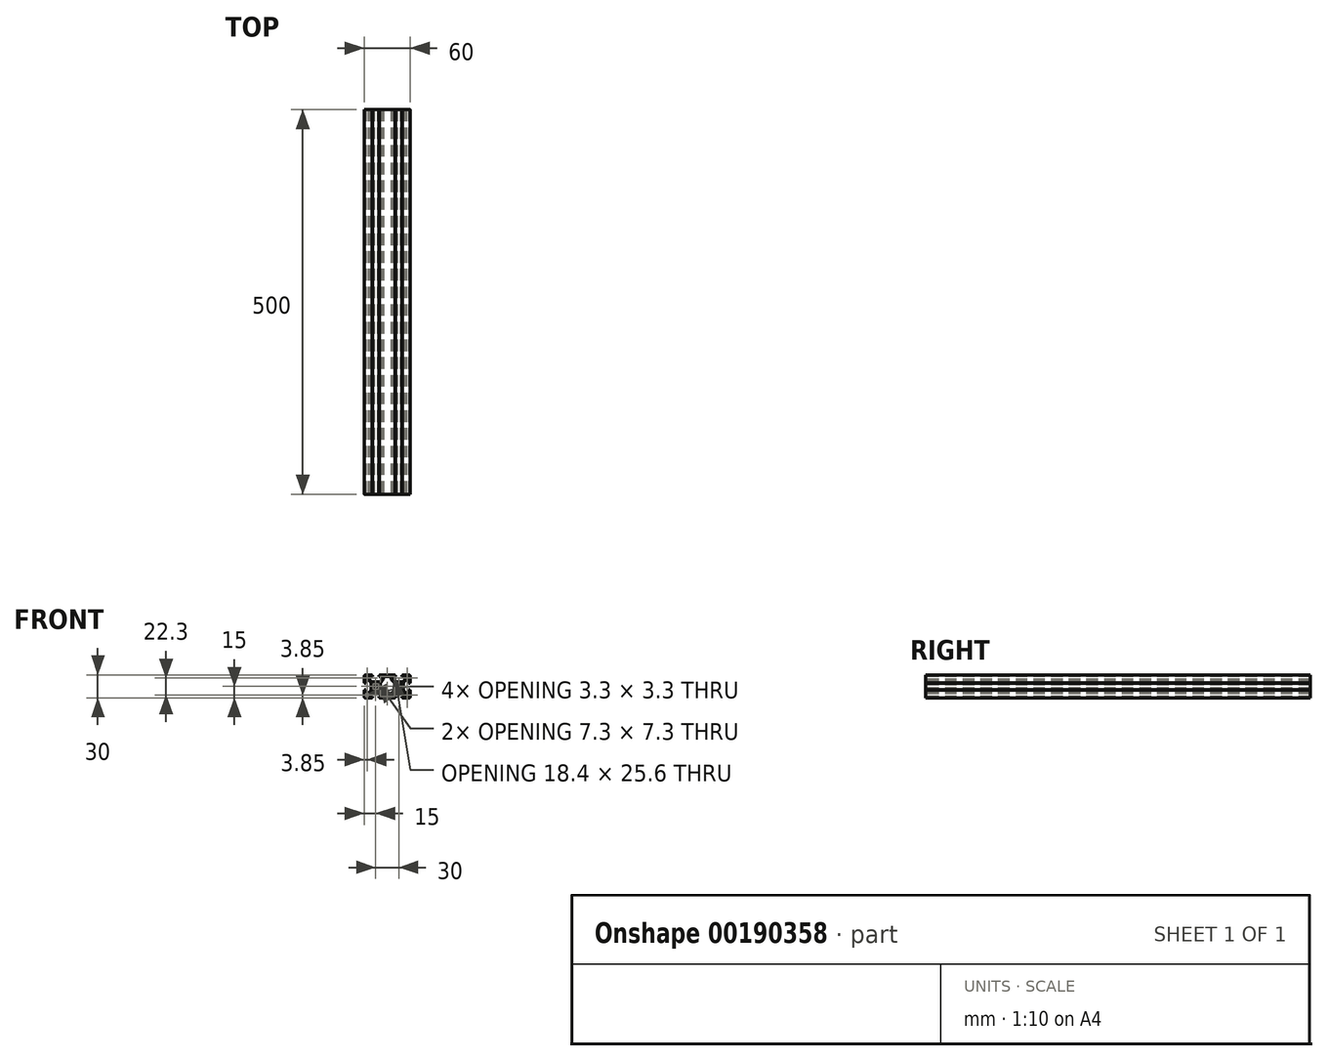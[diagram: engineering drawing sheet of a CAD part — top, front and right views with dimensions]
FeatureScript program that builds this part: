
annotation { "Feature Type Name" : "Feature", "Feature Type Description" : "" }
export const myFeature = defineFeature(function(context is Context, id is Id, definition is map)
    precondition{}
    {
        {
            var Q0;
            Q0=qCreatedBy(makeId("Front.planeOp"),FACE);
            var sketch = newSketch(context, id + "F0", { "sketchPlane" : qUnion([Q0])});
            skLineSegment(sketch, "E0.bottom", {"start": v(30, -15) * mm, "end": v(-30, -15) * mm});
            skLineSegment(sketch, "E0.top", {"start": v(30, 15) * mm, "end": v(-30, 15) * mm});
            skLineSegment(sketch, "E0.left", {"start": v(30, -15) * mm, "end": v(30, 15) * mm});
            skLineSegment(sketch, "E0.right", {"start": v(-30, -15) * mm, "end": v(-30, 15) * mm});
            skLineSegment(sketch, "E1", {"start": v(-30, -15) * mm, "end": v(30, 15) * mm, "construction": true});
            skSolve(sketch);
        }
        {
            var Q0;
            Q0 = qSketchRegion(id + "F0", true);
            extrude(context, id + "F1", {"entities" : qUnion([Q0]), "oppositeDirection" : true, "depth" : 500 * mm});
        }
        {
            var Q0;
            Q0=makeQuery(id+"F0.imprint","IMPRINT",FACE,{"disambiguationData":[TD([[makeQuery(id+"F0.imprint","IMPRINT",EDGE,{"derivedFrom":sQuery(id+"F0.wireOp",EDGE,"E0.bottom")}),-1.0]])]});
            var sketch = newSketch(context, id + "F2", { "sketchPlane" : qUnion([Q0])});
            skCircle(sketch, "E2", {"center": v(-15, 0) * mm, "radius": 3.65 * mm});
            skCircle(sketch, "E3.MirrorC", {"center": v(15, 0) * mm, "radius": 3.65 * mm});
            skSolve(sketch);
        }
        {
            var Q0;
            Q0 = qSketchRegion(id + "F2", true);
            extrude(context, id + "F3", {"entities" : qUnion([Q0]), "operationType" : NewBodyOperationType.REMOVE, "endBound" : BoundingType.THROUGH_ALL, "oppositeDirection" : true, "depth" : 25 * mm});
        }
        {
            var Q0;
            Q0=makeQuery(id+"F0.imprint","IMPRINT",FACE,{"disambiguationData":[TD([[makeQuery(id+"F0.imprint","IMPRINT",EDGE,{"derivedFrom":sQuery(id+"F0.wireOp",EDGE,"E0.bottom")}),-1.0]])]});
            var sketch = newSketch(context, id + "F4", { "sketchPlane" : qUnion([Q0])});
            skLineSegment(sketch, "E4", {"start": v(-15, 15) * mm, "end": v(-15, 0) * mm, "construction": true});
            skLineSegment(sketch, "E5", {"start": v(-15, 15) * mm, "end": v(-19, 15) * mm});
            skLineSegment(sketch, "E6", {"start": v(-19, 15) * mm, "end": v(-19, 12.8) * mm});
            skLineSegment(sketch, "E7", {"start": v(-19, 12.8) * mm, "end": v(-23, 12.8) * mm});
            skLineSegment(sketch, "E8", {"start": v(-23, 12.8) * mm, "end": v(-23, 8.8) * mm});
            skLineSegment(sketch, "E9", {"start": v(-20, 5.8) * mm, "end": v(-15, 5.8) * mm});
            skLineSegment(sketch, "E10.MirrorCS", {"start": v(-15, 15) * mm, "end": v(-11, 15) * mm});
            skLineSegment(sketch, "E11.MirrorCS", {"start": v(-11, 15) * mm, "end": v(-11, 12.8) * mm});
            skLineSegment(sketch, "E12.MirrorCS", {"start": v(-11, 12.8) * mm, "end": v(-7, 12.8) * mm});
            skLineSegment(sketch, "E13.MirrorCS", {"start": v(-10, 5.8) * mm, "end": v(-15, 5.8) * mm});
            skLineSegment(sketch, "E14.MirrorCS", {"start": v(-7, 12.8) * mm, "end": v(-7, 8.8) * mm});
            skLineSegment(sketch, "E15", {"start": v(0, 0) * mm, "end": v(0, 15) * mm, "construction": true});
            skLineSegment(sketch, "E16", {"start": v(0, 0) * mm, "end": v(-15, 0) * mm, "construction": true});
            skLineSegment(sketch, "E17", {"start": v(-20, 5.8) * mm, "end": v(-23, 8.8) * mm});
            skLineSegment(sketch, "E18.MirrorCS", {"start": v(-10, 5.8) * mm, "end": v(-7, 8.8) * mm});
            skLineSegment(sketch, "E19.MirrorCS", {"start": v(19, 15) * mm, "end": v(19, 12.8) * mm});
            skLineSegment(sketch, "E20.MirrorCS", {"start": v(11, 15) * mm, "end": v(11, 12.8) * mm});
            skLineSegment(sketch, "E21.MirrorCS", {"start": v(23, 12.8) * mm, "end": v(23, 8.8) * mm});
            skLineSegment(sketch, "E22.MirrorCS", {"start": v(20, 5.8) * mm, "end": v(15, 5.8) * mm});
            skLineSegment(sketch, "E23.MirrorCS", {"start": v(15, 15) * mm, "end": v(19, 15) * mm});
            skLineSegment(sketch, "E24.MirrorCS", {"start": v(7, 12.8) * mm, "end": v(7, 8.8) * mm});
            skLineSegment(sketch, "E25.MirrorCS", {"start": v(10, 5.8) * mm, "end": v(15, 5.8) * mm});
            skLineSegment(sketch, "E26.MirrorCS", {"start": v(19, 12.8) * mm, "end": v(23, 12.8) * mm});
            skLineSegment(sketch, "E27.MirrorCS", {"start": v(11, 12.8) * mm, "end": v(7, 12.8) * mm});
            skLineSegment(sketch, "E28.MirrorCS", {"start": v(15, 15) * mm, "end": v(11, 15) * mm});
            skLineSegment(sketch, "E29.MirrorCS", {"start": v(10, 5.8) * mm, "end": v(7, 8.8) * mm});
            skLineSegment(sketch, "E30.MirrorCS", {"start": v(20, 5.8) * mm, "end": v(23, 8.8) * mm});
            skLineSegment(sketch, "E31.1.0", {"start": v(20.8, 5) * mm, "end": v(23.8, 8) * mm});
            skLineSegment(sketch, "E31.1.1", {"start": v(30, 0) * mm, "end": v(30, -4) * mm});
            skLineSegment(sketch, "E31.1.2", {"start": v(27.8, -4) * mm, "end": v(27.8, -8) * mm});
            skLineSegment(sketch, "E31.1.3", {"start": v(27.8, -8) * mm, "end": v(23.8, -8) * mm});
            skLineSegment(sketch, "E31.1.4", {"start": v(30, 0) * mm, "end": v(30, 4) * mm});
            skLineSegment(sketch, "E31.1.5", {"start": v(27.8, 4) * mm, "end": v(27.8, 8) * mm});
            skLineSegment(sketch, "E31.1.6", {"start": v(20.8, 5) * mm, "end": v(20.8, 0) * mm});
            skLineSegment(sketch, "E31.1.7", {"start": v(27.8, 8) * mm, "end": v(23.8, 8) * mm});
            skLineSegment(sketch, "E31.1.8", {"start": v(20.8, -5) * mm, "end": v(20.8, 0) * mm});
            skLineSegment(sketch, "E31.1.9", {"start": v(20.8, -5) * mm, "end": v(23.8, -8) * mm});
            skLineSegment(sketch, "E31.1.10", {"start": v(27.8, 8) * mm, "end": v(23.8, 8) * mm});
            skLineSegment(sketch, "E31.1.11", {"start": v(20.8, -5) * mm, "end": v(20.8, 0) * mm});
            skLineSegment(sketch, "E31.1.12", {"start": v(20.8, 5) * mm, "end": v(20.8, 0) * mm});
            skLineSegment(sketch, "E31.1.13", {"start": v(30, 0) * mm, "end": v(30, -4) * mm});
            skLineSegment(sketch, "E31.1.14", {"start": v(27.8, 4) * mm, "end": v(27.8, 8) * mm});
            skLineSegment(sketch, "E31.1.15", {"start": v(27.8, -4) * mm, "end": v(27.8, -8) * mm});
            skLineSegment(sketch, "E31.1.16", {"start": v(27.8, -8) * mm, "end": v(23.8, -8) * mm});
            skLineSegment(sketch, "E31.1.17", {"start": v(30, 0) * mm, "end": v(30, 4) * mm});
            skLineSegment(sketch, "E31.1.18", {"start": v(30, 4) * mm, "end": v(27.8, 4) * mm});
            skLineSegment(sketch, "E31.1.19", {"start": v(30, -4) * mm, "end": v(27.8, -4) * mm});
            skLineSegment(sketch, "E31.1.20", {"start": v(30, 4) * mm, "end": v(27.8, 4) * mm});
            skLineSegment(sketch, "E31.1.21", {"start": v(30, -4) * mm, "end": v(27.8, -4) * mm});
            skLineSegment(sketch, "E31.2.0", {"start": v(20, -5.8) * mm, "end": v(23, -8.8) * mm});
            skLineSegment(sketch, "E31.2.1", {"start": v(15, -15) * mm, "end": v(11, -15) * mm});
            skLineSegment(sketch, "E31.2.2", {"start": v(11, -12.8) * mm, "end": v(7, -12.8) * mm});
            skLineSegment(sketch, "E31.2.3", {"start": v(7, -12.8) * mm, "end": v(7, -8.8) * mm});
            skLineSegment(sketch, "E31.2.4", {"start": v(15, -15) * mm, "end": v(19, -15) * mm});
            skLineSegment(sketch, "E31.2.5", {"start": v(19, -12.8) * mm, "end": v(23, -12.8) * mm});
            skLineSegment(sketch, "E31.2.6", {"start": v(20, -5.8) * mm, "end": v(15, -5.8) * mm});
            skLineSegment(sketch, "E31.2.7", {"start": v(23, -12.8) * mm, "end": v(23, -8.8) * mm});
            skLineSegment(sketch, "E31.2.8", {"start": v(10, -5.8) * mm, "end": v(15, -5.8) * mm});
            skLineSegment(sketch, "E31.2.9", {"start": v(10, -5.8) * mm, "end": v(7, -8.8) * mm});
            skLineSegment(sketch, "E31.2.10", {"start": v(23, -12.8) * mm, "end": v(23, -8.8) * mm});
            skLineSegment(sketch, "E31.2.11", {"start": v(10, -5.8) * mm, "end": v(15, -5.8) * mm});
            skLineSegment(sketch, "E31.2.12", {"start": v(20, -5.8) * mm, "end": v(15, -5.8) * mm});
            skLineSegment(sketch, "E31.2.13", {"start": v(15, -15) * mm, "end": v(11, -15) * mm});
            skLineSegment(sketch, "E31.2.14", {"start": v(19, -12.8) * mm, "end": v(23, -12.8) * mm});
            skLineSegment(sketch, "E31.2.15", {"start": v(11, -12.8) * mm, "end": v(7, -12.8) * mm});
            skLineSegment(sketch, "E31.2.16", {"start": v(7, -12.8) * mm, "end": v(7, -8.8) * mm});
            skLineSegment(sketch, "E31.2.17", {"start": v(15, -15) * mm, "end": v(19, -15) * mm});
            skLineSegment(sketch, "E31.2.18", {"start": v(19, -15) * mm, "end": v(19, -12.8) * mm});
            skLineSegment(sketch, "E31.2.19", {"start": v(11, -15) * mm, "end": v(11, -12.8) * mm});
            skLineSegment(sketch, "E31.2.20", {"start": v(19, -15) * mm, "end": v(19, -12.8) * mm});
            skLineSegment(sketch, "E31.2.21", {"start": v(11, -15) * mm, "end": v(11, -12.8) * mm});
            skPoint(sketch, "E31.center", {"position": v(15, 0) * mm});
            skLineSegment(sketch, "E31.anchor1", {"start": v(15, 0) * mm, "end": v(7, 8.8) * mm, "construction": true});
            skLineSegment(sketch, "E31.anchor2", {"start": v(15, 0) * mm, "end": v(23, -8.8) * mm, "construction": true});
            skLineSegment(sketch, "E32.MirrorCS", {"start": v(-20.8, 5) * mm, "end": v(-20.8, 0) * mm});
            skLineSegment(sketch, "E33.MirrorCS", {"start": v(-20.8, 5) * mm, "end": v(-23.8, 8) * mm});
            skLineSegment(sketch, "E34.MirrorCS", {"start": v(-27.8, 8) * mm, "end": v(-23.8, 8) * mm});
            skLineSegment(sketch, "E35.MirrorCS", {"start": v(-27.8, 4) * mm, "end": v(-27.8, 8) * mm});
            skLineSegment(sketch, "E36.MirrorCS", {"start": v(-30, 4) * mm, "end": v(-27.8, 4) * mm});
            skLineSegment(sketch, "E37.MirrorCS", {"start": v(-30, 0) * mm, "end": v(-30, 4) * mm});
            skLineSegment(sketch, "E38.MirrorCS", {"start": v(-30, 0) * mm, "end": v(-30, -4) * mm});
            skLineSegment(sketch, "E39.MirrorCS", {"start": v(-30, -4) * mm, "end": v(-27.8, -4) * mm});
            skLineSegment(sketch, "E40.MirrorCS", {"start": v(-27.8, -4) * mm, "end": v(-27.8, -8) * mm});
            skLineSegment(sketch, "E41.MirrorCS", {"start": v(-27.8, -8) * mm, "end": v(-23.8, -8) * mm});
            skLineSegment(sketch, "E42.MirrorCS", {"start": v(-20.8, -5) * mm, "end": v(-23.8, -8) * mm});
            skLineSegment(sketch, "E43.MirrorCS", {"start": v(-20.8, -5) * mm, "end": v(-20.8, 0) * mm});
            skLineSegment(sketch, "E44.MirrorCS", {"start": v(-19, -12.8) * mm, "end": v(-23, -12.8) * mm});
            skLineSegment(sketch, "E45.MirrorCS", {"start": v(-23, -12.8) * mm, "end": v(-23, -8.8) * mm});
            skLineSegment(sketch, "E46.MirrorCS", {"start": v(-11, -12.8) * mm, "end": v(-7, -12.8) * mm});
            skLineSegment(sketch, "E47.MirrorCS", {"start": v(-10, -5.8) * mm, "end": v(-15, -5.8) * mm});
            skLineSegment(sketch, "E48.MirrorCS", {"start": v(-20, -5.8) * mm, "end": v(-15, -5.8) * mm});
            skLineSegment(sketch, "E49.MirrorCS", {"start": v(-15, -15) * mm, "end": v(-19, -15) * mm});
            skLineSegment(sketch, "E50.MirrorCS", {"start": v(-19, -15) * mm, "end": v(-19, -12.8) * mm});
            skLineSegment(sketch, "E51.MirrorCS", {"start": v(-15, -15) * mm, "end": v(-11, -15) * mm});
            skLineSegment(sketch, "E52.MirrorCS", {"start": v(-11, -15) * mm, "end": v(-11, -12.8) * mm});
            skLineSegment(sketch, "E53.MirrorCS", {"start": v(-7, -12.8) * mm, "end": v(-7, -8.8) * mm});
            skLineSegment(sketch, "E54.MirrorCS", {"start": v(-20, -5.8) * mm, "end": v(-23, -8.8) * mm});
            skLineSegment(sketch, "E55.MirrorCS", {"start": v(-10, -5.8) * mm, "end": v(-7, -8.8) * mm});
            skLineSegment(sketch, "E56.MirrorCS", {"start": v(-9.2, 5) * mm, "end": v(-9.2, 0) * mm});
            skLineSegment(sketch, "E57.MirrorCS", {"start": v(-9.2, -5) * mm, "end": v(-9.2, 0) * mm});
            skLineSegment(sketch, "E58", {"start": v(-9.2, 5) * mm, "end": v(-5.3, 8.9) * mm});
            skLineSegment(sketch, "E59", {"start": v(-5.3, 8.9) * mm, "end": v(-5.3, 12.8) * mm});
            skLineSegment(sketch, "E60", {"start": v(-5.3, 12.8) * mm, "end": v(0, 12.8) * mm});
            skLineSegment(sketch, "E61.MirrorCS", {"start": v(-5.3, -12.8) * mm, "end": v(0, -12.8) * mm});
            skLineSegment(sketch, "E62.MirrorCS", {"start": v(-5.3, -8.9) * mm, "end": v(-5.3, -12.8) * mm});
            skLineSegment(sketch, "E63.MirrorCS", {"start": v(-9.2, -5) * mm, "end": v(-5.3, -8.9) * mm});
            skLineSegment(sketch, "E64.MirrorCS", {"start": v(5.3, 12.8) * mm, "end": v(0, 12.8) * mm});
            skLineSegment(sketch, "E65.MirrorCS", {"start": v(5.3, 8.9) * mm, "end": v(5.3, 12.8) * mm});
            skLineSegment(sketch, "E66.MirrorCS", {"start": v(9.2, 5) * mm, "end": v(5.3, 8.9) * mm});
            skLineSegment(sketch, "E67.MirrorCS", {"start": v(9.2, 5) * mm, "end": v(9.2, 0) * mm});
            skLineSegment(sketch, "E68.MirrorCS", {"start": v(9.2, -5) * mm, "end": v(9.2, 0) * mm});
            skLineSegment(sketch, "E69.MirrorCS", {"start": v(9.2, -5) * mm, "end": v(5.3, -8.9) * mm});
            skLineSegment(sketch, "E70.MirrorCS", {"start": v(5.3, -12.8) * mm, "end": v(0, -12.8) * mm});
            skLineSegment(sketch, "E71.MirrorCS", {"start": v(5.3, -8.9) * mm, "end": v(5.3, -12.8) * mm});
            skSolve(sketch);
        }
        {
            var Q0;
            Q0 = qSketchRegion(id + "F4", true);
            extrude(context, id + "F5", {"entities" : qUnion([Q0]), "operationType" : NewBodyOperationType.REMOVE, "endBound" : BoundingType.THROUGH_ALL, "oppositeDirection" : true, "depth" : 25 * mm});
        }
        {
            var Q0;
            Q0=makeQuery(id+"F1.opExtrude","SWEPT_EDGE",EDGE,{"disambiguationData":[OSD([sQuery(id+"F0.wireOp",EDGE,"E0.top"),sQuery(id+"F0.wireOp",EDGE,"E0.right")])]});
            var Q1;
            Q1=makeQuery(id+"F1.opExtrude","SWEPT_EDGE",EDGE,{"disambiguationData":[OSD([sQuery(id+"F0.wireOp",EDGE,"E0.top"),sQuery(id+"F0.wireOp",EDGE,"E0.left")])]});
            var Q2;
            Q2=makeQuery(id+"F1.opExtrude","SWEPT_EDGE",EDGE,{"disambiguationData":[OSD([sQuery(id+"F0.wireOp",EDGE,"E0.bottom"),sQuery(id+"F0.wireOp",EDGE,"E0.left")])]});
            var Q3;
            Q3=makeQuery(id+"F1.opExtrude","SWEPT_EDGE",EDGE,{"disambiguationData":[OSD([sQuery(id+"F0.wireOp",EDGE,"E0.bottom"),sQuery(id+"F0.wireOp",EDGE,"E0.right")])]});
            fillet(context, id + "F6", {"entities" : qUnion([Q0, Q1, Q2, Q3]), "radius" : 2 * mm, "tangentPropagation" : true, "allowEdgeOverflow" : false});
        }
        {
            var Q0;
            Q0=makeQuery(id+"F1.opExtrude","CAP_FACE",FACE,{"disambiguationData":[OSD([sQuery(id+"F0.wireOp",EDGE,"E0.bottom"),sQuery(id+"F0.wireOp",EDGE,"E0.top"),sQuery(id+"F0.wireOp",EDGE,"E0.left"),sQuery(id+"F0.wireOp",EDGE,"E0.right")])],"isStart":true});
            var sketch = newSketch(context, id + "F7", { "sketchPlane" : qUnion([Q0])});
            skLineSegment(sketch, "E72", {"start": v(-24.5, 9.5) * mm, "end": v(-27.8, 9.5) * mm});
            skLineSegment(sketch, "E73", {"start": v(-27.8, 9.5) * mm, "end": v(-27.8, 11.8) * mm});
            skLineSegment(sketch, "E74", {"start": v(-26.8, 12.8) * mm, "end": v(-24.5, 12.8) * mm});
            skLineSegment(sketch, "E75", {"start": v(-24.5, 12.8) * mm, "end": v(-24.5, 9.5) * mm});
            skPoint(sketch, "E76.visualSharp", {"position": v(-27.8, 12.8) * mm});
            skArc(sketch, "E76.filletArc", {"start": v(-26.8, 12.8) * mm, "mid": v(-27.5, 12.5) * mm, "end": v(-27.8, 11.8) * mm});
            skLineSegment(sketch, "E77", {"start": v(0, 0) * mm, "end": v(0, 17.26) * mm, "construction": true});
            skPoint(sketch, "E77.endSnap0", {"position": v(0, 15) * mm});
            skLineSegment(sketch, "E78", {"start": v(0, 0) * mm, "end": v(-33.03, 0) * mm, "construction": true});
            skLineSegment(sketch, "E79.MirrorCS", {"start": v(24.5, 12.8) * mm, "end": v(24.5, 9.5) * mm});
            skArc(sketch, "E80.MirrorCS", {"start": v(26.8, 12.8) * mm, "mid": v(27.5, 12.5) * mm, "end": v(27.8, 11.8) * mm});
            skPoint(sketch, "E81.MirrorP", {"position": v(27.8, 12.8) * mm});
            skLineSegment(sketch, "E82.MirrorCS", {"start": v(24.5, 9.5) * mm, "end": v(27.8, 9.5) * mm});
            skLineSegment(sketch, "E83.MirrorCS", {"start": v(27.8, 9.5) * mm, "end": v(27.8, 11.8) * mm});
            skLineSegment(sketch, "E84.MirrorCS", {"start": v(26.8, 12.8) * mm, "end": v(24.5, 12.8) * mm});
            skArc(sketch, "E85.MirrorCS", {"start": v(26.8, -12.8) * mm, "mid": v(27.5, -12.5) * mm, "end": v(27.8, -11.8) * mm});
            skLineSegment(sketch, "E86.MirrorCS", {"start": v(-27.8, -9.5) * mm, "end": v(-27.8, -11.8) * mm});
            skArc(sketch, "E87.MirrorCS", {"start": v(-26.8, -12.8) * mm, "mid": v(-27.5, -12.5) * mm, "end": v(-27.8, -11.8) * mm});
            skLineSegment(sketch, "E88.MirrorCS", {"start": v(-24.5, -12.8) * mm, "end": v(-24.5, -9.5) * mm});
            skPoint(sketch, "E89.MirrorP", {"position": v(27.8, -12.8) * mm});
            skPoint(sketch, "E90.MirrorP", {"position": v(-27.8, -12.8) * mm});
            skPoint(sketch, "E91.MirrorP", {"position": v(0, -15) * mm});
            skLineSegment(sketch, "E92.MirrorCS", {"start": v(26.8, -12.8) * mm, "end": v(24.5, -12.8) * mm});
            skLineSegment(sketch, "E93.MirrorCS", {"start": v(-24.5, -9.5) * mm, "end": v(-27.8, -9.5) * mm});
            skLineSegment(sketch, "E94.MirrorCS", {"start": v(27.8, -9.5) * mm, "end": v(27.8, -11.8) * mm});
            skLineSegment(sketch, "E95.MirrorCS", {"start": v(24.5, -9.5) * mm, "end": v(27.8, -9.5) * mm});
            skLineSegment(sketch, "E96.MirrorCS", {"start": v(24.5, -12.8) * mm, "end": v(24.5, -9.5) * mm});
            skLineSegment(sketch, "E97.MirrorCS", {"start": v(-26.8, -12.8) * mm, "end": v(-24.5, -12.8) * mm});
            skSolve(sketch);
        }
        {
            var Q0;
            Q0 = qSketchRegion(id + "F7", true);
            extrude(context, id + "F8", {"entities" : qUnion([Q0]), "operationType" : NewBodyOperationType.REMOVE, "endBound" : BoundingType.THROUGH_ALL, "oppositeDirection" : true, "depth" : 25 * mm});
        }
        {
            var Q0;
            Q0=makeQuery(id+"F1.opExtrude","CAP_FACE",FACE,{"disambiguationData":[OSD([sQuery(id+"F0.wireOp",EDGE,"E0.bottom"),sQuery(id+"F0.wireOp",EDGE,"E0.top"),sQuery(id+"F0.wireOp",EDGE,"E0.left"),sQuery(id+"F0.wireOp",EDGE,"E0.right")])],"isStart":true});
            var sketch = newSketch(context, id + "F9", { "sketchPlane" : qUnion([Q0])});
            skLineSegment(sketch, "E98", {"start": v(-15, 0) * mm, "end": v(-15, 5.8) * mm, "construction": true});
            skLineSegment(sketch, "E99", {"start": v(-15, 0) * mm, "end": v(-20.8, 5.8) * mm, "construction": true});
            skLineSegment(sketch, "E100", {"start": v(-17.95, 2.15) * mm, "end": v(-18.64, 2.84) * mm});
            skLineSegment(sketch, "E101", {"start": v(-17.22, 2.9) * mm, "end": v(-17.9, 3.58) * mm});
            skPoint(sketch, "E101.startSnap0", {"position": v(-17.9, 2.9) * mm});
            skPoint(sketch, "E101.endSnap0", {"position": v(-17.9, 2.9) * mm});
            skLineSegment(sketch, "E102", {"start": v(-17.9, 3.58) * mm, "end": v(-18.64, 2.84) * mm});
            skLineSegment(sketch, "E103", {"start": v(-17.95, 2.15) * mm, "end": v(-17.22, 2.9) * mm});
            skLineSegment(sketch, "E104.1.0", {"start": v(-17.15, -2.95) * mm, "end": v(-17.84, -3.64) * mm});
            skLineSegment(sketch, "E104.1.1", {"start": v(-18.58, -2.9) * mm, "end": v(-17.84, -3.64) * mm});
            skLineSegment(sketch, "E104.1.2", {"start": v(-17.9, -2.22) * mm, "end": v(-18.58, -2.9) * mm});
            skLineSegment(sketch, "E104.1.3", {"start": v(-17.15, -2.95) * mm, "end": v(-17.9, -2.22) * mm});
            skLineSegment(sketch, "E104.2.0", {"start": v(-12.05, -2.15) * mm, "end": v(-11.36, -2.84) * mm});
            skLineSegment(sketch, "E104.2.1", {"start": v(-12.1, -3.58) * mm, "end": v(-11.36, -2.84) * mm});
            skLineSegment(sketch, "E104.2.2", {"start": v(-12.78, -2.9) * mm, "end": v(-12.1, -3.58) * mm});
            skLineSegment(sketch, "E104.2.3", {"start": v(-12.05, -2.15) * mm, "end": v(-12.78, -2.9) * mm});
            skLineSegment(sketch, "E104.3.0", {"start": v(-12.85, 2.95) * mm, "end": v(-12.16, 3.64) * mm});
            skLineSegment(sketch, "E104.3.1", {"start": v(-11.42, 2.9) * mm, "end": v(-12.16, 3.64) * mm});
            skLineSegment(sketch, "E104.3.2", {"start": v(-12.1, 2.22) * mm, "end": v(-11.42, 2.9) * mm});
            skLineSegment(sketch, "E104.3.3", {"start": v(-12.85, 2.95) * mm, "end": v(-12.1, 2.22) * mm});
            skPoint(sketch, "E104.center", {"position": v(-15, 0) * mm});
            skLineSegment(sketch, "E105", {"start": v(0, 0) * mm, "end": v(0, 16.82) * mm, "construction": true});
            skPoint(sketch, "E105.endSnap0", {"position": v(0, 15) * mm});
            skLineSegment(sketch, "E106.MirrorCS", {"start": v(12.1, 2.22) * mm, "end": v(11.42, 2.9) * mm});
            skLineSegment(sketch, "E107.MirrorCS", {"start": v(11.42, 2.9) * mm, "end": v(12.16, 3.64) * mm});
            skLineSegment(sketch, "E108.MirrorCS", {"start": v(12.85, 2.95) * mm, "end": v(12.16, 3.64) * mm});
            skLineSegment(sketch, "E109.MirrorCS", {"start": v(12.85, 2.95) * mm, "end": v(12.1, 2.22) * mm});
            skLineSegment(sketch, "E110.MirrorCS", {"start": v(17.95, 2.15) * mm, "end": v(17.22, 2.9) * mm});
            skLineSegment(sketch, "E111.MirrorCS", {"start": v(17.22, 2.9) * mm, "end": v(17.9, 3.58) * mm});
            skLineSegment(sketch, "E112.MirrorCS", {"start": v(17.9, 3.58) * mm, "end": v(18.64, 2.84) * mm});
            skLineSegment(sketch, "E113.MirrorCS", {"start": v(17.95, 2.15) * mm, "end": v(18.64, 2.84) * mm});
            skLineSegment(sketch, "E114.MirrorCS", {"start": v(18.58, -2.9) * mm, "end": v(17.84, -3.64) * mm});
            skLineSegment(sketch, "E115.MirrorCS", {"start": v(17.9, -2.22) * mm, "end": v(18.58, -2.9) * mm});
            skLineSegment(sketch, "E116.MirrorCS", {"start": v(17.15, -2.95) * mm, "end": v(17.9, -2.22) * mm});
            skLineSegment(sketch, "E117.MirrorCS", {"start": v(17.15, -2.95) * mm, "end": v(17.84, -3.64) * mm});
            skLineSegment(sketch, "E118.MirrorCS", {"start": v(12.05, -2.15) * mm, "end": v(11.36, -2.84) * mm});
            skLineSegment(sketch, "E119.MirrorCS", {"start": v(12.05, -2.15) * mm, "end": v(12.78, -2.9) * mm});
            skLineSegment(sketch, "E120.MirrorCS", {"start": v(12.78, -2.9) * mm, "end": v(12.1, -3.58) * mm});
            skLineSegment(sketch, "E121.MirrorCS", {"start": v(12.1, -3.58) * mm, "end": v(11.36, -2.84) * mm});
            skSolve(sketch);
        }
        {
            var Q0;
            Q0 = qSketchRegion(id + "F9", true);
            extrude(context, id + "F10", {"entities" : qUnion([Q0]), "operationType" : NewBodyOperationType.REMOVE, "endBound" : BoundingType.THROUGH_ALL, "oppositeDirection" : true, "depth" : 25 * mm});
        }
        {
            var Q0;
            Q0=makeQuery(id+"F1.opExtrude","CAP_FACE",FACE,{"disambiguationData":[OSD([sQuery(id+"F0.wireOp",EDGE,"E0.bottom"),sQuery(id+"F0.wireOp",EDGE,"E0.top"),sQuery(id+"F0.wireOp",EDGE,"E0.left"),sQuery(id+"F0.wireOp",EDGE,"E0.right")])],"isStart":true});
            var sketch = newSketch(context, id + "F11", { "sketchPlane" : qUnion([Q0])});
            skLineSegment(sketch, "E122.bottom", {"start": v(11, 15) * mm, "end": v(10.2, 15) * mm});
            skLineSegment(sketch, "E122.top", {"start": v(11, 14.2) * mm, "end": v(10.2, 14.2) * mm});
            skLineSegment(sketch, "E122.left", {"start": v(11, 15) * mm, "end": v(11, 14.2) * mm});
            skLineSegment(sketch, "E122.right", {"start": v(10.2, 15) * mm, "end": v(10.2, 14.2) * mm});
            skLineSegment(sketch, "E123.bottom", {"start": v(19, 15) * mm, "end": v(19.8, 15) * mm});
            skLineSegment(sketch, "E123.top", {"start": v(19, 14.2) * mm, "end": v(19.8, 14.2) * mm});
            skLineSegment(sketch, "E123.left", {"start": v(19, 15) * mm, "end": v(19, 14.2) * mm});
            skLineSegment(sketch, "E123.right", {"start": v(19.8, 15) * mm, "end": v(19.8, 14.2) * mm});
            skLineSegment(sketch, "E124.1.0", {"start": v(30, -4) * mm, "end": v(30, -4.8) * mm});
            skLineSegment(sketch, "E124.1.1", {"start": v(29.2, -4) * mm, "end": v(29.2, -4.8) * mm});
            skLineSegment(sketch, "E124.1.2", {"start": v(30, 4) * mm, "end": v(30, 4.8) * mm});
            skLineSegment(sketch, "E124.1.3", {"start": v(29.2, 4) * mm, "end": v(29.2, 4.8) * mm});
            skLineSegment(sketch, "E124.1.4", {"start": v(30, 4) * mm, "end": v(29.2, 4) * mm});
            skLineSegment(sketch, "E124.1.5", {"start": v(30, 4.8) * mm, "end": v(29.2, 4.8) * mm});
            skLineSegment(sketch, "E124.1.6", {"start": v(30, -4.8) * mm, "end": v(29.2, -4.8) * mm});
            skLineSegment(sketch, "E124.1.7", {"start": v(30, -4) * mm, "end": v(29.2, -4) * mm});
            skLineSegment(sketch, "E124.2.0", {"start": v(11, -15) * mm, "end": v(10.2, -15) * mm});
            skLineSegment(sketch, "E124.2.1", {"start": v(11, -14.2) * mm, "end": v(10.2, -14.2) * mm});
            skLineSegment(sketch, "E124.2.2", {"start": v(19, -15) * mm, "end": v(19.8, -15) * mm});
            skLineSegment(sketch, "E124.2.3", {"start": v(19, -14.2) * mm, "end": v(19.8, -14.2) * mm});
            skLineSegment(sketch, "E124.2.4", {"start": v(19, -15) * mm, "end": v(19, -14.2) * mm});
            skLineSegment(sketch, "E124.2.5", {"start": v(19.8, -15) * mm, "end": v(19.8, -14.2) * mm});
            skLineSegment(sketch, "E124.2.6", {"start": v(10.2, -15) * mm, "end": v(10.2, -14.2) * mm});
            skLineSegment(sketch, "E124.2.7", {"start": v(11, -15) * mm, "end": v(11, -14.2) * mm});
            skPoint(sketch, "E124.center", {"position": v(15, 0) * mm});
            skLineSegment(sketch, "E124.anchor1", {"start": v(15, 0) * mm, "end": v(10.2, 14.2) * mm, "construction": true});
            skLineSegment(sketch, "E124.anchor2", {"start": v(15, 0) * mm, "end": v(19.8, -14.2) * mm, "construction": true});
            skLineSegment(sketch, "E125", {"start": v(0, 0) * mm, "end": v(0, 17.97) * mm, "construction": true});
            skPoint(sketch, "E125.endSnap0", {"position": v(0, 15) * mm});
            skLineSegment(sketch, "E126.MirrorCS", {"start": v(-11, 14.2) * mm, "end": v(-10.2, 14.2) * mm});
            skLineSegment(sketch, "E127.MirrorCS", {"start": v(-19.8, 15) * mm, "end": v(-19.8, 14.2) * mm});
            skLineSegment(sketch, "E128.MirrorCS", {"start": v(-19, 15) * mm, "end": v(-19, 14.2) * mm});
            skLineSegment(sketch, "E129.MirrorCS", {"start": v(-19, 14.2) * mm, "end": v(-19.8, 14.2) * mm});
            skLineSegment(sketch, "E130.MirrorCS", {"start": v(-19, 15) * mm, "end": v(-19.8, 15) * mm});
            skLineSegment(sketch, "E131.MirrorCS", {"start": v(-10.2, 15) * mm, "end": v(-10.2, 14.2) * mm});
            skLineSegment(sketch, "E132.MirrorCS", {"start": v(-11, 15) * mm, "end": v(-11, 14.2) * mm});
            skLineSegment(sketch, "E133.MirrorCS", {"start": v(-11, 15) * mm, "end": v(-10.2, 15) * mm});
            skLineSegment(sketch, "E134.MirrorCS", {"start": v(-30, 4) * mm, "end": v(-29.2, 4) * mm});
            skLineSegment(sketch, "E135.MirrorCS", {"start": v(-29.2, 4) * mm, "end": v(-29.2, 4.8) * mm});
            skLineSegment(sketch, "E136.MirrorCS", {"start": v(-30, 4) * mm, "end": v(-30, 4.8) * mm});
            skLineSegment(sketch, "E137.MirrorCS", {"start": v(-29.2, -4) * mm, "end": v(-29.2, -4.8) * mm});
            skLineSegment(sketch, "E138.MirrorCS", {"start": v(-30, -4) * mm, "end": v(-30, -4.8) * mm});
            skLineSegment(sketch, "E139.MirrorCS", {"start": v(-30, 4.8) * mm, "end": v(-29.2, 4.8) * mm});
            skLineSegment(sketch, "E140.MirrorCS", {"start": v(-30, -4.8) * mm, "end": v(-29.2, -4.8) * mm});
            skLineSegment(sketch, "E141.MirrorCS", {"start": v(-30, -4) * mm, "end": v(-29.2, -4) * mm});
            skLineSegment(sketch, "E142.MirrorCS", {"start": v(-19, -14.2) * mm, "end": v(-19.8, -14.2) * mm});
            skLineSegment(sketch, "E143.MirrorCS", {"start": v(-11, -15) * mm, "end": v(-11, -14.2) * mm});
            skLineSegment(sketch, "E144.MirrorCS", {"start": v(-11, -14.2) * mm, "end": v(-10.2, -14.2) * mm});
            skLineSegment(sketch, "E145.MirrorCS", {"start": v(-11, -15) * mm, "end": v(-10.2, -15) * mm});
            skLineSegment(sketch, "E146.MirrorCS", {"start": v(-10.2, -15) * mm, "end": v(-10.2, -14.2) * mm});
            skLineSegment(sketch, "E147.MirrorCS", {"start": v(-19.8, -15) * mm, "end": v(-19.8, -14.2) * mm});
            skLineSegment(sketch, "E148.MirrorCS", {"start": v(-19, -15) * mm, "end": v(-19, -14.2) * mm});
            skLineSegment(sketch, "E149.MirrorCS", {"start": v(-19, -15) * mm, "end": v(-19.8, -15) * mm});
            skSolve(sketch);
        }
        {
            var Q0;
            Q0 = qSketchRegion(id + "F11", true);
            extrude(context, id + "F12", {"entities" : qUnion([Q0]), "operationType" : NewBodyOperationType.REMOVE, "endBound" : BoundingType.THROUGH_ALL, "oppositeDirection" : true, "depth" : 25 * mm});
        }
    });
